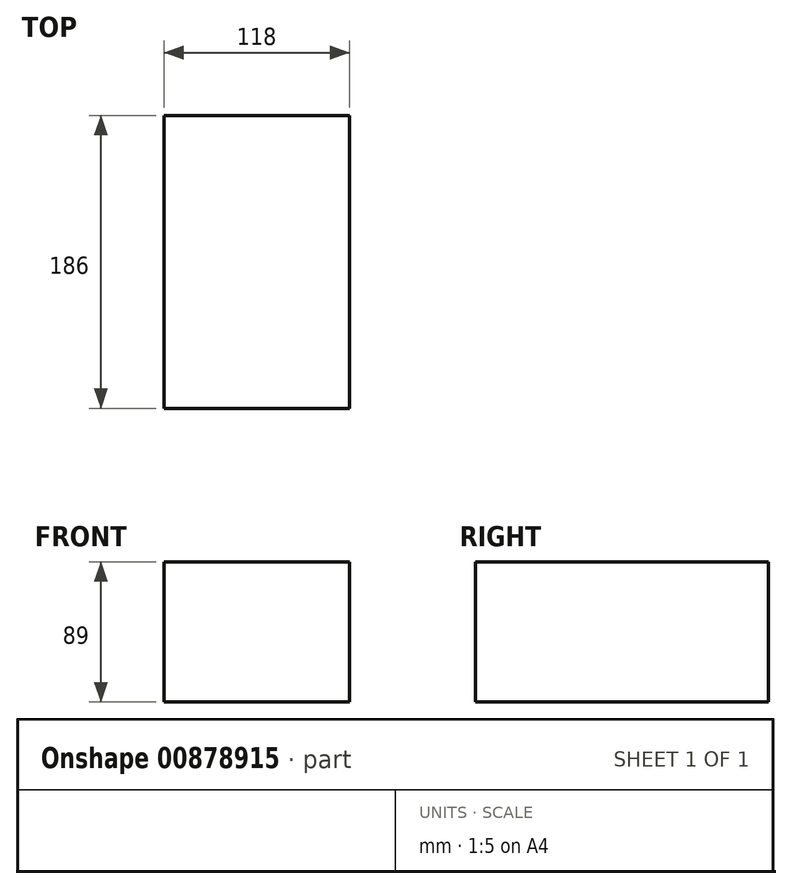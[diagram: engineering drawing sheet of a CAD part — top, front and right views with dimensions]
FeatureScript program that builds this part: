
annotation { "Feature Type Name" : "Feature", "Feature Type Description" : "" }
export const myFeature = defineFeature(function(context is Context, id is Id, definition is map)
    precondition{}
    {
        {
            var Q0;
            Q0=qCreatedBy(makeId("Top.planeOp"),FACE);
            var sketch = newSketch(context, id + "F0", { "sketchPlane" : qUnion([Q0])});
            skLineSegment(sketch, "E0.bottom", {"start": v(-60.9, 97.59) * mm, "end": v(57.1, 97.59) * mm});
            skLineSegment(sketch, "E0.top", {"start": v(-60.9, -88.41) * mm, "end": v(57.1, -88.41) * mm});
            skLineSegment(sketch, "E0.left", {"start": v(-60.9, 97.59) * mm, "end": v(-60.9, -88.41) * mm});
            skLineSegment(sketch, "E0.right", {"start": v(57.1, 97.59) * mm, "end": v(57.1, -88.41) * mm});
            skSolve(sketch);
        }
        {
            var Q0;
            Q0=makeQuery(id+"F0.imprint","IMPRINT",FACE,{"disambiguationData":[TD([[makeQuery(id+"F0.imprint","IMPRINT",EDGE,{"derivedFrom":sQuery(id+"F0.wireOp",EDGE,"E0.bottom")}),-1.0]])]});
            extrude(context, id + "F1", {"entities" : qUnion([Q0]), "depth" : 89 * mm, "offsetDistance" : 25 * mm});
        }
    });
